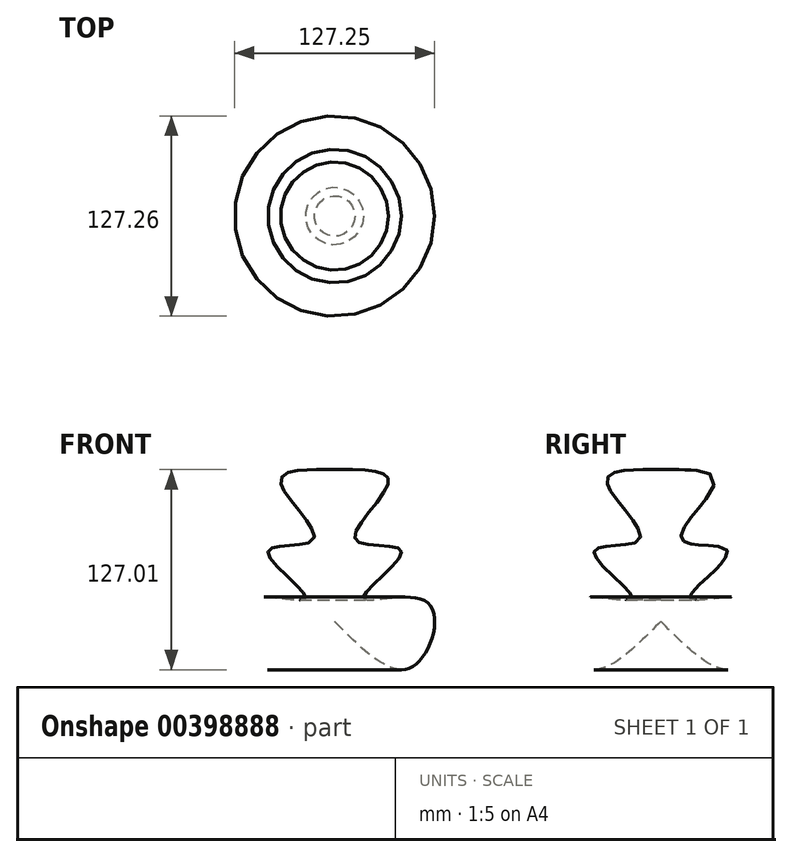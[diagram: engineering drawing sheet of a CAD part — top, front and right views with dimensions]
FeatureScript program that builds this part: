
annotation { "Feature Type Name" : "Feature", "Feature Type Description" : "" }
export const myFeature = defineFeature(function(context is Context, id is Id, definition is map)
    precondition{}
    {
        {
            var Q0;
            Q0=qCreatedBy(makeId("Front.planeOp"),FACE);
            var sketch = newSketch(context, id + "F0", { "sketchPlane" : qUnion([Q0])});
            skLineSegment(sketch, "E0", {"start": v(-63.1, 44.18) * mm, "end": v(-63.1, -51.96) * mm});
            skFitSpline(sketch, "E1", {"points": [v(-63.1, 44.18) * mm, v(-28.9, 36.42) * mm, v(-49.7, 0) * mm, v(-20.8, -7.41) * mm, v(-44.77, -36.9) * mm, v(-4.58, -39.74) * mm, v(-13.4, -80.71) * mm, v(-63.1, -51.96) * mm], "startDerivative": vector(397.94, 9.69) * mm, "endDerivative": vector(-318.39, 323.54) * mm});
            skSolve(sketch);
        }
        {
            var Q0;
            Q0=makeQuery(id+"F0.imprint","IMPRINT",FACE,{"disambiguationData":[TD([[makeQuery(id+"F0.imprint","IMPRINT",EDGE,{"derivedFrom":sQuery(id+"F0.wireOp",EDGE,"E0")}),1.0]])]});
            var Q1;
            Q1=sQuery(id+"F0.wireOp",EDGE,"E0");
            revolve(context, id + "F1", {"entities" : qUnion([Q0]), "axis" : qUnion([Q1]), "revolveType" : RevolveType.FULL});
        }
    });
